# Revit family: CleanLine serisi duş kanalları için Geberit montaj seti, girişte 90–220 mm şap yüksekliği için_PRO_170941
name_source: partatom
category: Plumbing Fixtures
revit_build: Autodesk Revit 2018 (Build: 20190510_1515(x64)
units: mm (PartAtom-declared; Revit-internal decimal feet)

## family parameters
Always vertical = Yes
Cut with Voids When Loaded = No
OmniClass Number = 23.70.50.21.24
OmniClass Title = Waste Water Drains
Part Type = Normal
Room Calculation Point = Yes
Round Connector Dimension = Use Diameter
Shared = No
Work Plane-Based = No

## types (1)
- 154.150.00.1 CleanLine serisi duş kanalları için Geberit montaj seti, girişte 90–220 mm şap yüksekliği için
    Application purposes = CleanLine serisi Geberit duş kanallarında drenaj için
Kompozit contalar için
Girişte ≥ 90 mm şap yükseklikleri için
    Application range = Floor drainage system
    Article number key = 154.150.00.1
    B = 130 mm
    BIM Content Version = GEB MG 1.2
    BIM Content revision date = 2020.04.30
    Brand = Geberit
    CW Connection = No
    Characteristics = EN 1253-3 uyarınca kalite kontrollü
Önceden monte edilmiş izolasyon bezi
Sızdırmazlık sistemleri bağlantısı için 10 cm çevreleyen izolasyon bezi
Akustik izolasyon ve sifon bağlantısı için EPS ana ünite
    Connection diameter 1 = 50 mm  [stored 0.164042 ft]
    Description = CleanLine serisi duş kanalları için Geberit montaj seti, girişte 90–220 mm şap yüksekliği için
    Drenaj kapasitesi = 0.8 L/s
    EAN code basic data = 4025416364498
    GEB_culture = tr-TR
    GEB_generic_description = installation set for shower channels
    GEB_generic_manufacturer = generic
    GEB_generic_model = horizontal outlet
    GEB_imperial_engineering = No
    GEB_key_rules = 1000 [Articles.ArticlesList.Key]
2000 [Name], d[ATT_10935]mm
3000 [ATT_10673]
    GEB_metric_engineering = Yes
    GEB_pimversion = 22.02.12
    GEB_processing_type = T
    GEB_reference = PRO_170941
    GEB_size_max = 220 mm  [stored 0.721785 ft]
    GEB_size_min = 90 mm
    GEB_translations = {"ATT_10673":"EAN code basic data","applicationPurposes":"Application purposes","application_range":"Application range","brandName":"Brand","characteristics":"Characteristics","content_creator":"BIM Content creator","content_date_changed":"BIM Content revision date","content_version":"BIM Content Version","key 1000":"Article number key","name":"Name","productBrand":"Product brand","type":"Type","GEB_connection_diameter1":"Connection diameter 1","angle":"Angle","ATT_10753":"Drenaj kapasitesi","fixed_material":"Main material","fixed_material_01":"Main material 01","ATT_10931":"B","ATT_10935":"d, ø","ATT_10951":"H","ATT_10952":"h","ATT_10953":"H1","ATT_10966":"L","ATT_10969":"L1","GEB_accessories":"Accessories"}
    GEB_use_DN = Yes
    H = 90 mm
    H1 = 9-22 cm
    HW Connection = No
    IfcDescription = CleanLine serisi duş kanalları için Geberit montaj seti, girişte 90–220 mm şap yüksekliği için
    IfcExportAs = IfcSanitaryTerminal
    IfcExportType = USERDEFINED
    L = 300 mm
    L1 = 358 mm
    LOD300 = No
    LOD400 = Yes
    Main material = Geberit_Plastic, White
    Main material 01 = Geberit_PE-HD, Black
    Manufacturer = Geberit
    Model = d50
    Name = CleanLine serisi duş kanalları için Geberit montaj seti, girişte 90–220 mm şap yüksekliği için
    Type = d50
    Vent Connection = No
    WFU = 0
    Waste Connection = Yes
    d, ø = 50 mm  [stored 0.164042 ft]
    h = 42 mm  [stored 0.137795 ft]

note: [stored X ft] marks values corroborated as IEEE doubles in the binary element streams (Revit-internal decimal feet)

## geometry (parser evidence)
native form markers: Blend x2
no freeform markers — native parametric forms only
